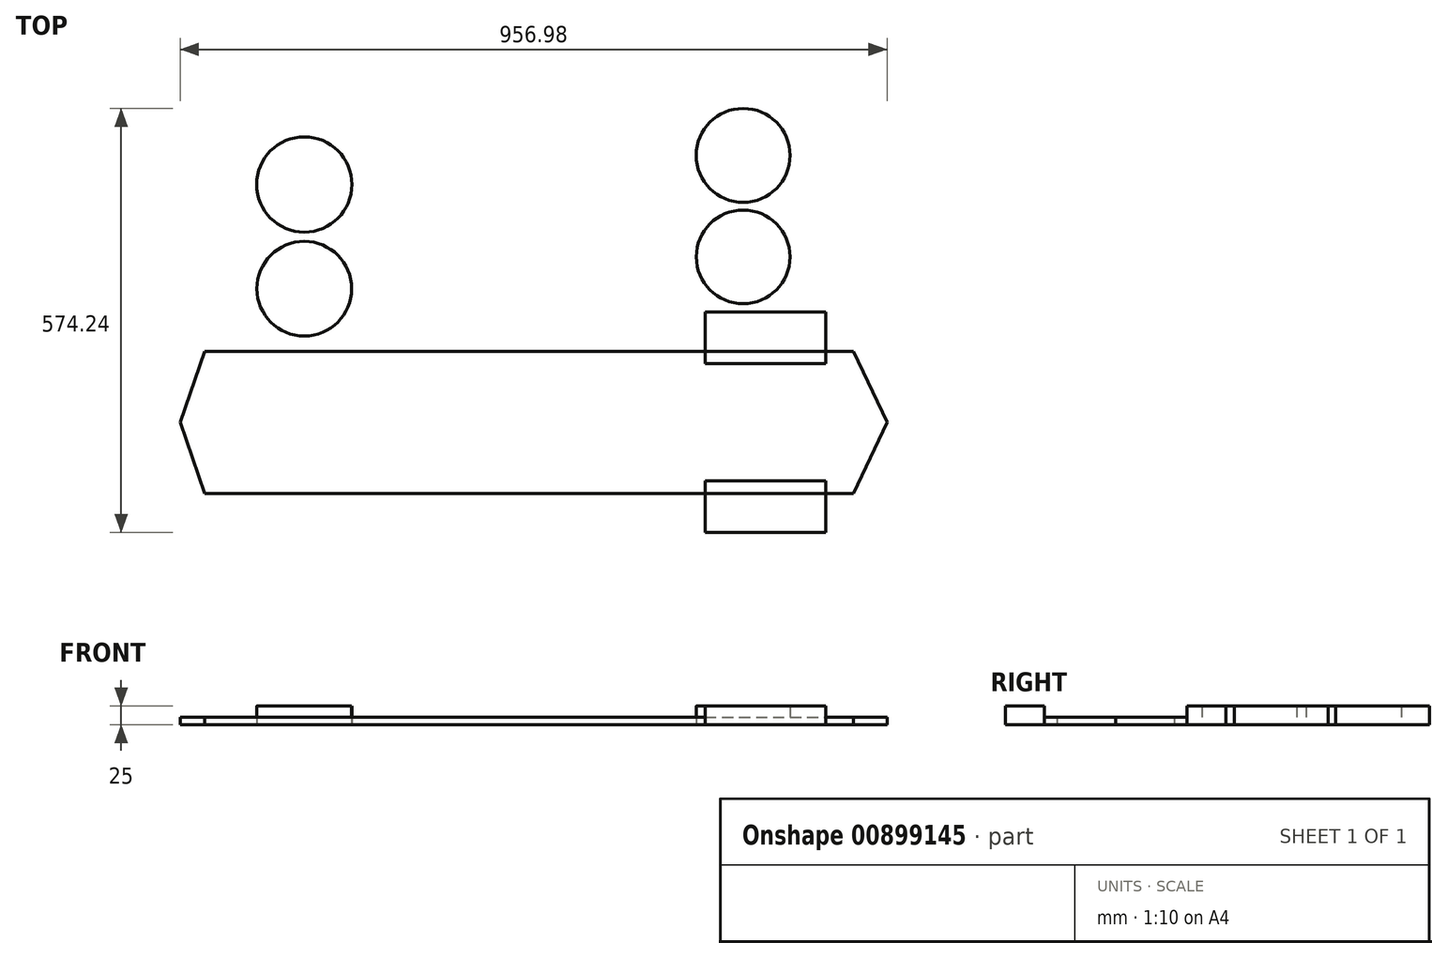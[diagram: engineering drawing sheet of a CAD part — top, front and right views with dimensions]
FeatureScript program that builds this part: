
annotation { "Feature Type Name" : "Feature", "Feature Type Description" : "" }
export const myFeature = defineFeature(function(context is Context, id is Id, definition is map)
    precondition{}
    {
        {
            var Q0;
            Q0=qCreatedBy(makeId("Top.planeOp"),FACE);
            var sketch = newSketch(context, id + "F0", { "sketchPlane" : qUnion([Q0])});
            skCircle(sketch, "E0", {"center": v(-396.43, 339.36) * mm, "radius": 64.49 * mm});
            skCircle(sketch, "E1", {"center": v(-396.32, 198.23) * mm, "radius": 64.1 * mm});
            skCircle(sketch, "E2", {"center": v(197.74, 241.35) * mm, "radius": 63.42 * mm});
            skCircle(sketch, "E3", {"center": v(197.71, 378.74) * mm, "radius": 63.52 * mm});
            skLineSegment(sketch, "E4.bottom", {"start": v(-531.22, 113.62) * mm, "end": v(347.22, 113.62) * mm});
            skLineSegment(sketch, "E5", {"start": v(-564.33, 17.38) * mm, "end": v(-531.22, 113.62) * mm});
            skLineSegment(sketch, "E6", {"start": v(347.22, 113.62) * mm, "end": v(392.65, 17.38) * mm});
            skPoint(sketch, "E7.orphan", {"position": v(392.65, 113.62) * mm});
            skPoint(sketch, "E8.orphan", {"position": v(-564.33, 113.62) * mm});
            skLineSegment(sketch, "E9.bottom", {"start": v(146.28, 166.74) * mm, "end": v(309.5, 166.74) * mm});
            skLineSegment(sketch, "E9.top", {"start": v(146.28, 96.68) * mm, "end": v(309.5, 96.68) * mm});
            skLineSegment(sketch, "E9.left", {"start": v(146.28, 166.74) * mm, "end": v(146.28, 96.68) * mm});
            skLineSegment(sketch, "E9.right", {"start": v(309.5, 166.74) * mm, "end": v(309.5, 96.68) * mm});
            skLineSegment(sketch, "E10", {"start": v(-564.33, 17.38) * mm, "end": v(392.65, 17.38) * mm, "construction": true});
            skLineSegment(sketch, "E11.MirrorCS", {"start": v(309.5, -131.98) * mm, "end": v(309.5, -61.92) * mm});
            skLineSegment(sketch, "E12.MirrorCS", {"start": v(146.28, -61.92) * mm, "end": v(309.5, -61.92) * mm});
            skLineSegment(sketch, "E13.MirrorCS", {"start": v(146.28, -131.98) * mm, "end": v(309.5, -131.98) * mm});
            skLineSegment(sketch, "E14.MirrorCS", {"start": v(146.28, -131.98) * mm, "end": v(146.28, -61.92) * mm});
            skCircle(sketch, "E15.MirrorC", {"center": v(-396.32, -163.47) * mm, "radius": 64.1 * mm});
            skCircle(sketch, "E16.MirrorC", {"center": v(197.74, -206.59) * mm, "radius": 63.42 * mm});
            skCircle(sketch, "E17.MirrorC", {"center": v(-396.43, -304.6) * mm, "radius": 64.49 * mm});
            skCircle(sketch, "E18.MirrorC", {"center": v(197.71, -343.97) * mm, "radius": 63.52 * mm});
            skLineSegment(sketch, "E19.MirrorCS", {"start": v(347.22, -78.85) * mm, "end": v(392.65, 17.38) * mm});
            skLineSegment(sketch, "E20.MirrorCS", {"start": v(-564.33, 17.38) * mm, "end": v(-531.22, -78.85) * mm});
            skLineSegment(sketch, "E21.MirrorCS", {"start": v(-531.22, -78.85) * mm, "end": v(347.22, -78.85) * mm});
            skSolve(sketch);
        }
        {
            var Q0;
            Q0=makeQuery(id+"F0.imprint","IMPRINT",FACE,{"disambiguationData":[TD([[makeQuery(id+"F0.imprint","IMPRINT",EDGE,{"derivedFrom":sQuery(id+"F0.wireOp",EDGE,"E1")}),1.0]])]});
            var Q1;
            Q1=makeQuery(id+"F0.imprint","IMPRINT",FACE,{"disambiguationData":[TD([[makeQuery(id+"F0.imprint","IMPRINT",EDGE,{"derivedFrom":sQuery(id+"F0.wireOp",EDGE,"E0")}),1.0]])]});
            var Q2;
            Q2=makeQuery(id+"F0.imprint","IMPRINT",FACE,{"disambiguationData":[TD([[makeQuery(id+"F0.imprint","IMPRINT",EDGE,{"derivedFrom":sQuery(id+"F0.wireOp",EDGE,"E3")}),1.0]])]});
            var Q3;
            Q3=makeQuery(id+"F0.imprint","IMPRINT",FACE,{"disambiguationData":[TD([[makeQuery(id+"F0.imprint","IMPRINT",EDGE,{"derivedFrom":sQuery(id+"F0.wireOp",EDGE,"E2")}),1.0]])]});
            var Q4;
            Q4=makeQuery(id+"F0.imprint","IMPRINT",FACE,{"disambiguationData":[TD([[makeQuery(id+"F0.imprint","IMPRINT",EDGE,{"derivedFrom":sQuery(id+"F0.wireOp",EDGE,"E16.MirrorC")}),-1.0]])]});
            var Q5;
            Q5=makeQuery(id+"F0.imprint","IMPRINT",FACE,{"disambiguationData":[TD([[makeQuery(id+"F0.imprint","IMPRINT",EDGE,{"derivedFrom":sQuery(id+"F0.wireOp",EDGE,"E18.MirrorC")}),-1.0]])]});
            var Q6;
            Q6=makeQuery(id+"F0.imprint","IMPRINT",FACE,{"disambiguationData":[TD([[makeQuery(id+"F0.imprint","IMPRINT",EDGE,{"derivedFrom":sQuery(id+"F0.wireOp",EDGE,"E15.MirrorC")}),-1.0]])]});
            var Q7;
            Q7=makeQuery(id+"F0.imprint","IMPRINT",FACE,{"disambiguationData":[TD([[makeQuery(id+"F0.imprint","IMPRINT",EDGE,{"derivedFrom":sQuery(id+"F0.wireOp",EDGE,"E17.MirrorC")}),-1.0]])]});
            var Q8;
            {var subQ5=sQuery(id+"F0.wireOp",EDGE,"E9.bottom");Q8=makeQuery(id+"F0.imprint","IMPRINT",FACE,{"disambiguationData":[TD([[makeQuery(id+"F0.imprint","IMPRINT",EDGE,{"derivedFrom":subQ5}),-1.0]])]});}
            var Q9;
            {var subQ0=sQuery(id+"F0.wireOp",EDGE,"E13.MirrorCS");Q9=makeQuery(id+"F0.imprint","IMPRINT",FACE,{"disambiguationData":[TD([[makeQuery(id+"F0.imprint","IMPRINT",EDGE,{"derivedFrom":subQ0}),1.0]])]});}
            extrude(context, id + "F1", {"entities" : qUnion([Q0, Q1, Q2, Q3, Q4, Q5, Q6, Q7, Q8, Q9]), "depth" : 25 * mm, "offsetDistance" : 25 * mm});
        }
        {
            var Q0;
            {var subQ12=sQuery(id+"F0.wireOp",EDGE,"E5");Q0=makeQuery(id+"F0.imprint","IMPRINT",FACE,{"disambiguationData":[TD([[makeQuery(id+"F0.imprint","IMPRINT",EDGE,{"derivedFrom":subQ12}),-1.0]])]});}
            extrude(context, id + "F2", {"entities" : qUnion([Q0]), "depth" : 10 * mm, "offsetDistance" : 25 * mm});
        }
    });
